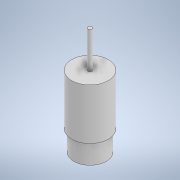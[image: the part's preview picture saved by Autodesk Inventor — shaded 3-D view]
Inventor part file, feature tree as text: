
AUTODESK INVENTOR PART (.ipt)
format: ipt  version: 2022 (Build 260153000, 153)  size: 118,272 bytes
history: native  units: mm
features: sketch x5, extrude x4
ambient origin geometry x8: Origin, YZ Plane, XZ Plane, XY Plane, X Axis, Y Axis, Z Axis, Center Point
bodies: Solid1 (feature_tree)
feature tree (9):
  extrude  "Extrusion1"  Depth=18.0mm
  extrude  "Extrusion2"  Depth=25.0mm
  extrude  "Extrusion3"  Depth=10.0mm
  extrude  "Extrusion4"  Depth=4.0mm
  sketch  "Sketch5"  dims[d11=18.0mm d12=0.0mm]
  sketch  "Sketch1"  dims[d0=20.0mm d1=18.0mm]
  sketch  "Sketch2"  dims[d2=25.0mm d3=0.0mm d4=16.0mm]
  sketch  "Sketch3"  dims[d5=10.0mm d6=0.0mm d7=5.0mm]
  sketch  "Sketch4"  dims[d8=4.0mm d9=0.0mm d10=2.0mm]
